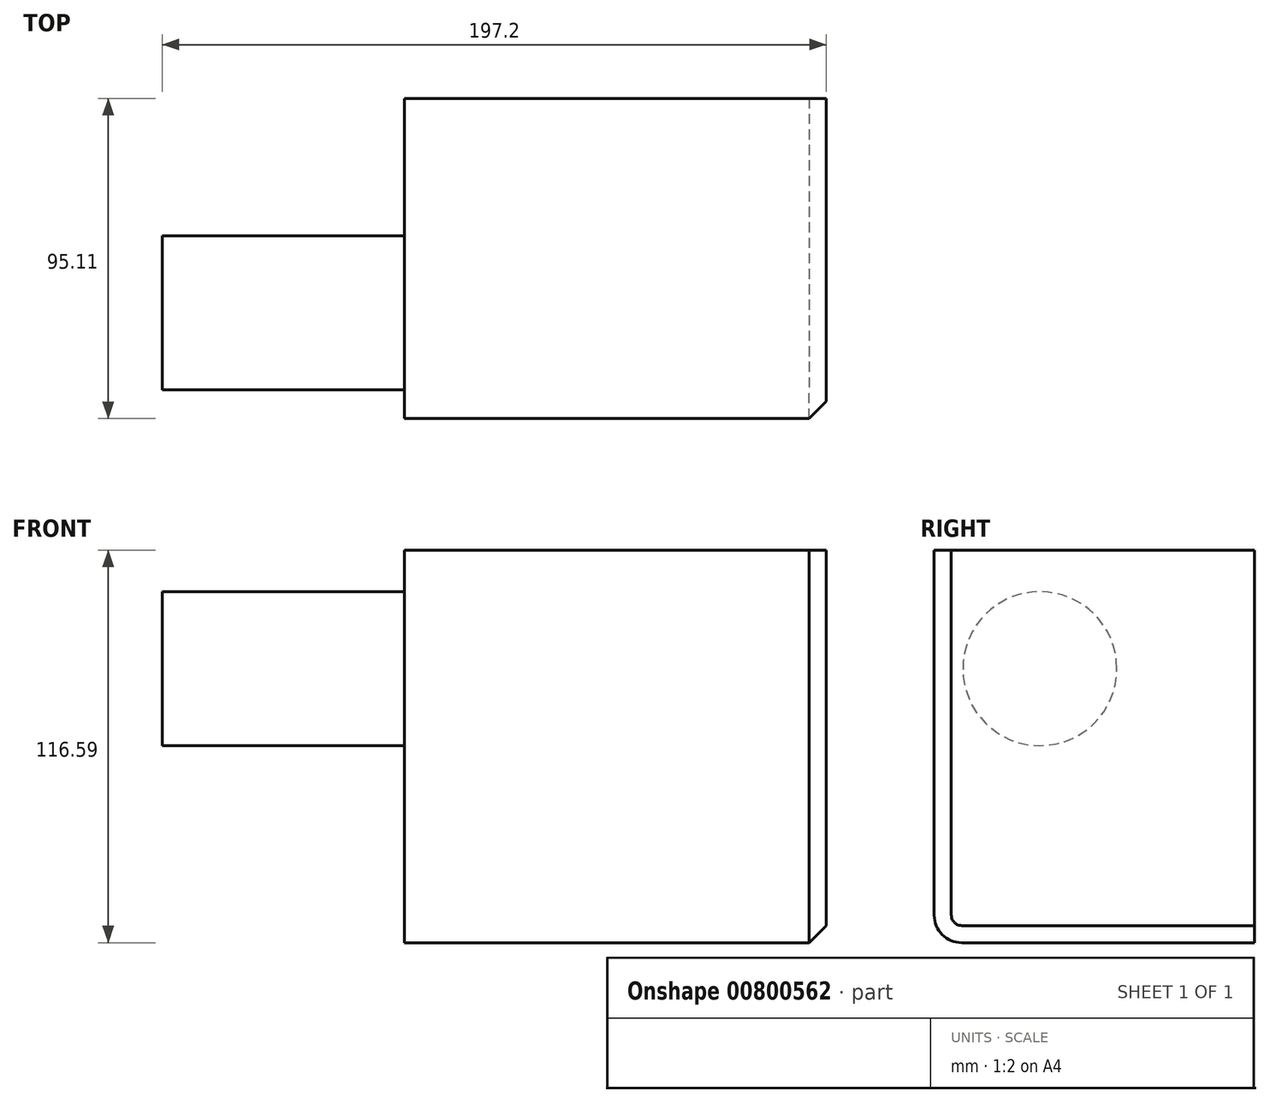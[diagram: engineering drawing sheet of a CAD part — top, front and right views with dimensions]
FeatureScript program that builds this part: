
annotation { "Feature Type Name" : "Feature", "Feature Type Description" : "" }
export const myFeature = defineFeature(function(context is Context, id is Id, definition is map)
    precondition{}
    {
        {
            var Q0;
            Q0=qCreatedBy(makeId("Front.planeOp"),FACE);
            var sketch = newSketch(context, id + "F0", { "sketchPlane" : qUnion([Q0])});
            skLineSegment(sketch, "E0.bottom", {"start": v(-61.4, 56.43) * mm, "end": v(63.9, 56.43) * mm});
            skLineSegment(sketch, "E0.top", {"start": v(-61.4, -60.16) * mm, "end": v(63.9, -60.16) * mm});
            skLineSegment(sketch, "E0.left", {"start": v(-61.4, 56.43) * mm, "end": v(-61.4, -60.16) * mm});
            skLineSegment(sketch, "E0.right", {"start": v(63.9, 56.43) * mm, "end": v(63.9, -60.16) * mm});
            skSolve(sketch);
        }
        {
            var Q0;
            Q0 = qSketchRegion(id + "F0", true);
            extrude(context, id + "F1", {"entities" : qUnion([Q0]), "depth" : 95.1 * mm, "offsetDistance" : 25.4 * mm});
        }
        {
            var Q0;
            Q0=makeQuery(id+"F1.opExtrude","CAP_EDGE",EDGE,{"disambiguationData":[OSD([sQuery(id+"F0.wireOp",EDGE,"E0.top")])],"isStart":false});
            fillet(context, id + "F2", {"entities" : qUnion([Q0]), "radius" : 8.21 * mm, "tangentPropagation" : true, "allowEdgeOverflow" : false});
        }
        {
            var Q0;
            Q0=makeQuery(id+"F1.opExtrude","CAP_EDGE",EDGE,{"disambiguationData":[OSD([sQuery(id+"F0.wireOp",EDGE,"E0.right")])],"isStart":false});
            chamfer(context, id + "F3", {"entities" : qUnion([Q0]), "width" : 5.08 * mm, "tangentPropagation" : true});
        }
        {
            var Q0;
            Q0=makeQuery(id+"F1.opExtrude","SWEPT_FACE",FACE,{"disambiguationData":[OSD([sQuery(id+"F0.wireOp",EDGE,"E0.left")])]});
            var sketch = newSketch(context, id + "F4", { "sketchPlane" : qUnion([Q0])});
            skCircle(sketch, "E1", {"center": v(63.73, 21.2) * mm, "radius": 22.85 * mm});
            skSolve(sketch);
        }
        {
            var Q0;
            Q0=makeQuery(id+"F4.imprint","IMPRINT",FACE,{"disambiguationData":[TD([[makeQuery(id+"F4.imprint","IMPRINT",EDGE,{"derivedFrom":sQuery(id+"F4.wireOp",EDGE,"E1")}),1.0]])]});
            extrude(context, id + "F5", {"entities" : qUnion([Q0]), "operationType" : NewBodyOperationType.ADD, "depth" : 71.9 * mm, "offsetDistance" : 25.4 * mm});
        }
    });
